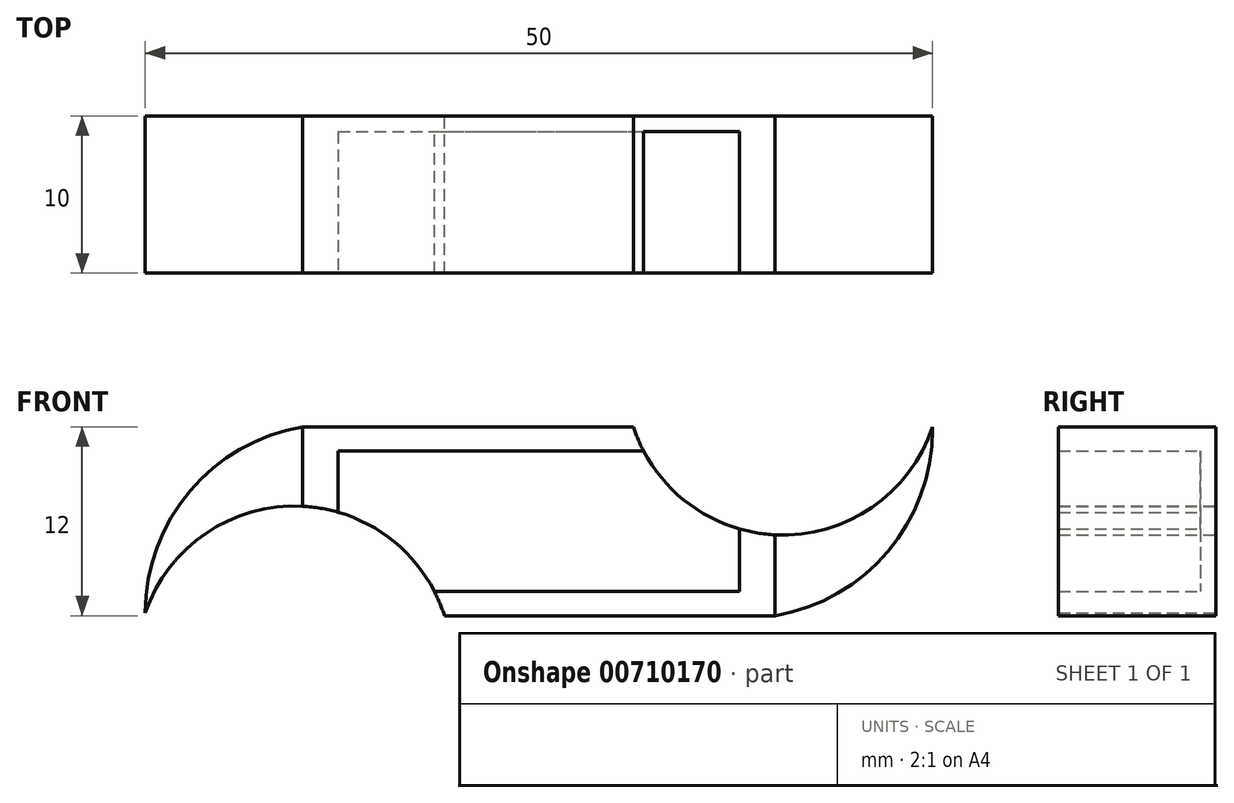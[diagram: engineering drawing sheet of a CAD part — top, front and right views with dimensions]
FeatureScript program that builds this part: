
annotation { "Feature Type Name" : "Feature", "Feature Type Description" : "" }
export const myFeature = defineFeature(function(context is Context, id is Id, definition is map)
    precondition{}
    {
        {
            var Q0;
            Q0=qCreatedBy(makeId("Top.planeOp"),FACE);
            var sketch = newSketch(context, id + "F0", { "sketchPlane" : qUnion([Q0])});
            skLineSegment(sketch, "E0", {"start": v(0, 0) * mm, "end": v(25.5, 0) * mm});
            skLineSegment(sketch, "E1", {"start": v(25.5, 0) * mm, "end": v(25.5, 8.9) * mm});
            skLineSegment(sketch, "E2", {"start": v(25.5, 8.9) * mm, "end": v(0, 8.9) * mm});
            skLineSegment(sketch, "E3", {"start": v(0, 8.9) * mm, "end": v(0, 0) * mm});
            skSolve(sketch);
        }
        {
            var Q0;
            Q0=makeQuery(id+"F0.imprint","IMPRINT",FACE,{"disambiguationData":[TD([[makeQuery(id+"F0.imprint","IMPRINT",EDGE,{"derivedFrom":sQuery(id+"F0.wireOp",EDGE,"E0")}),1.0]])]});
            extrude(context, id + "F1", {"entities" : qUnion([Q0]), "depth" : 8.9 * mm, "offsetDistance" : 25 * mm});
        }
        {
            var Q0;
            Q0=makeQuery(id+"F1.opExtrude","SWEPT_FACE",FACE,{"disambiguationData":[OSD([sQuery(id+"F0.wireOp",EDGE,"E0")])]});
            var sketch = newSketch(context, id + "F2", { "sketchPlane" : qUnion([Q0])});
            skLineSegment(sketch, "E4.bottom", {"start": v(-2.25, 10.45) * mm, "end": v(27.75, 10.45) * mm});
            skLineSegment(sketch, "E4.top", {"start": v(-2.25, -1.55) * mm, "end": v(27.75, -1.55) * mm});
            skLineSegment(sketch, "E4.left", {"start": v(-2.25, 10.45) * mm, "end": v(-2.25, -1.55) * mm});
            skLineSegment(sketch, "E4.right", {"start": v(27.75, 10.45) * mm, "end": v(27.75, -1.55) * mm});
            skPoint(sketch, "E4.middle", {"position": v(12.75, 4.45) * mm});
            skSolve(sketch);
        }
        {
            var Q0;
            {var subQ0=sQuery(id+"F0.wireOp",EDGE,"E0");Q0=makeQuery(id+"F2.imprint","IMPRINT",FACE,{"disambiguationData":[TD([[makeQuery(id+"F2.imprint","IMPRINT",EDGE,{"derivedFrom":makeQuery(id+"F1.opExtrude","CAP_EDGE",EDGE,{"disambiguationData":[OSD([subQ0])],"isStart":true})}),1.0]])]});}
            var Q1;
            Q1=makeQuery(id+"F2.imprint","IMPRINT",FACE,{"disambiguationData":[TD([[makeQuery(id+"F2.imprint","IMPRINT",EDGE,{"derivedFrom":sQuery(id+"F2.wireOp",EDGE,"E4.bottom")}),-1.0]])]});
            extrude(context, id + "F3", {"entities" : qUnion([Q0, Q1]), "oppositeDirection" : true, "depth" : 10 * mm, "offsetDistance" : 25 * mm});
        }
        {
            var Q0;
            Q0=makeQuery(id+"F1.opExtrude","SWEPT_FACE",FACE,{"disambiguationData":[OSD([sQuery(id+"F0.wireOp",EDGE,"E0")])]});
            extrude(context, id + "F4", {"entities" : qUnion([Q0]), "operationType" : NewBodyOperationType.REMOVE, "oppositeDirection" : true, "depth" : 9 * mm, "offsetDistance" : 25 * mm});
        }
        {
            var Q0;
            Q0=makeQuery(id+"F3.opExtrude","SWEPT_FACE",FACE,{"disambiguationData":[OSD([sQuery(id+"F2.wireOp",EDGE,"E4.left")])]});
            extrude(context, id + "F5", {"entities" : qUnion([Q0]), "depth" : 10 * mm, "offsetDistance" : 25 * mm});
        }
        {
            var Q0;
            Q0=makeQuery(id+"F3.opExtrude","SWEPT_FACE",FACE,{"disambiguationData":[OSD([sQuery(id+"F2.wireOp",EDGE,"E4.right")])]});
            extrude(context, id + "F6", {"entities" : qUnion([Q0]), "depth" : 10 * mm, "offsetDistance" : 25 * mm});
        }
        {
            var Q0;
            Q0=makeQuery(id+"F3.opExtrude","SWEPT_FACE",FACE,{"disambiguationData":[OSD([sQuery(id+"F2.wireOp",EDGE,"E4.bottom")])]});
            var sketch = newSketch(context, id + "F7", { "sketchPlane" : qUnion([Q0])});
            skLineSegment(sketch, "E5", {"start": v(12.75, 0) * mm, "end": v(18.75, 0) * mm});
            skLineSegment(sketch, "E6", {"start": v(18.75, 0) * mm, "end": v(18.75, 10) * mm});
            skLineSegment(sketch, "E7", {"start": v(18.75, 10) * mm, "end": v(12.75, 10) * mm});
            skLineSegment(sketch, "E8", {"start": v(12.75, 10) * mm, "end": v(6.75, 10) * mm});
            skLineSegment(sketch, "E9", {"start": v(6.75, 10) * mm, "end": v(6.75, 0) * mm});
            skLineSegment(sketch, "E10", {"start": v(12.75, 0) * mm, "end": v(6.75, 0) * mm});
            skSolve(sketch);
        }
        {
            var Q0;
            Q0=makeQuery(id+"F3.opExtrude","SWEPT_FACE",FACE,{"disambiguationData":[OSD([sQuery(id+"F2.wireOp",EDGE,"E4.top")])]});
            var sketch = newSketch(context, id + "F8", { "sketchPlane" : qUnion([Q0])});
            skLineSegment(sketch, "E11", {"start": v(12.75, -10) * mm, "end": v(18.75, -10) * mm});
            skLineSegment(sketch, "E12", {"start": v(18.75, -10) * mm, "end": v(18.75, 0) * mm});
            skLineSegment(sketch, "E13", {"start": v(12.75, 0) * mm, "end": v(18.75, 0) * mm});
            skLineSegment(sketch, "E14", {"start": v(12.75, 0) * mm, "end": v(6.75, 0) * mm});
            skLineSegment(sketch, "E15", {"start": v(6.75, 0) * mm, "end": v(6.75, -10) * mm});
            skLineSegment(sketch, "E16", {"start": v(6.75, -10) * mm, "end": v(12.75, -10) * mm});
            skSolve(sketch);
        }
        {
            var Q0;
            Q0=makeQuery(id+"FosGmJq5SILQGFZ_5.opExtrude","CAP_EDGE",EDGE,{"disambiguationData":[OSD([sQuery(id+"F8.wireOp",EDGE,"E15")])],"isStart":false});
            var Q1;
            Q1=makeQuery(id+"F5.opExtrude","CAP_EDGE",EDGE,{"disambiguationData":[OSD([sQuery(id+"F2.wireOp",EDGE,"E4.bottom"),sQuery(id+"F2.wireOp",EDGE,"E4.left")])],"isStart":false});
            var Q2;
            Q2=makeQuery(id+"FqWK5za6CKHgtiD_4.opExtrude","CAP_EDGE",EDGE,{"disambiguationData":[OSD([sQuery(id+"F7.wireOp",EDGE,"E6")])],"isStart":false});
            var Q3;
            Q3=makeQuery(id+"F6.opExtrude","CAP_EDGE",EDGE,{"disambiguationData":[OSD([sQuery(id+"F2.wireOp",EDGE,"E4.top"),sQuery(id+"F2.wireOp",EDGE,"E4.right")])],"isStart":false});
            fillet(context, id + "F9", {"entities" : qUnion([Q0, Q1, Q2, Q3]), "radius" : 12 * mm, "tangentPropagation" : true, "allowEdgeOverflow" : false});
        }
        {
            var Q0;
            Q0=makeQuery(id+"FosGmJq5SILQGFZ_5.boolean.opBoolean","MERGE",FACE,{"derivedFrom":[makeQuery(id+"FqWK5za6CKHgtiD_4.boolean.opBoolean","MERGE",FACE,{"derivedFrom":[makeQuery(id+"F3.opExtrude","CAP_FACE",FACE,{"disambiguationData":[OSD([sQuery(id+"F2.wireOp",EDGE,"E4.bottom"),sQuery(id+"F2.wireOp",EDGE,"E4.top"),sQuery(id+"F2.wireOp",EDGE,"E4.left"),sQuery(id+"F2.wireOp",EDGE,"E4.right")])],"isStart":false}),makeQuery(id+"FqWK5za6CKHgtiD_4.opExtrude","SWEPT_FACE",FACE,{"disambiguationData":[OSD([sQuery(id+"F7.wireOp",EDGE,"E7"),sQuery(id+"F7.wireOp",EDGE,"E8")])]})]}),makeQuery(id+"FosGmJq5SILQGFZ_5.opExtrude","SWEPT_FACE",FACE,{"disambiguationData":[OSD([sQuery(id+"F8.wireOp",EDGE,"E11"),sQuery(id+"F8.wireOp",EDGE,"E16")])]})]});
            var sketch = newSketch(context, id + "F10", { "sketchPlane" : qUnion([Q0])});
            skPoint(sketch, "E17.0", {"position": v(-12.75, 10.45) * mm});
            skLineSegment(sketch, "E18", {"start": v(-18.75, 10.45) * mm, "end": v(-18.75, -1.55) * mm});
            skLineSegment(sketch, "E19", {"start": v(-18.75, -1.55) * mm, "end": v(-6.75, -1.55) * mm});
            skLineSegment(sketch, "E20", {"start": v(-6.75, -1.55) * mm, "end": v(-6.75, 10.45) * mm});
            skLineSegment(sketch, "E21", {"start": v(-6.75, 10.45) * mm, "end": v(-18.75, 10.45) * mm});
            skLineSegment(sketch, "E22.0.0", {"start": v(12.25, -1.55) * mm, "end": v(12.25, -1.38) * mm});
            skArc(sketch, "E22.0.1", {"start": v(12.25, -1.38) * mm, "mid": v(9.42, 6.36) * mm, "end": v(2.25, 10.45) * mm});
            skLineSegment(sketch, "E22.0.2", {"start": v(2.25, 10.45) * mm, "end": v(2.25, -1.55) * mm});
            skLineSegment(sketch, "E22.0.3", {"start": v(2.25, -1.55) * mm, "end": v(12.25, -1.55) * mm});
            skLineSegment(sketch, "E23.0.0", {"start": v(-37.75, 10.45) * mm, "end": v(-37.75, 10.28) * mm});
            skArc(sketch, "E23.0.1", {"start": v(-37.75, 10.28) * mm, "mid": v(-34.92, 2.54) * mm, "end": v(-27.75, -1.55) * mm});
            skLineSegment(sketch, "E23.0.2", {"start": v(-27.75, -1.55) * mm, "end": v(-27.75, 10.45) * mm});
            skLineSegment(sketch, "E23.0.3", {"start": v(-27.75, 10.45) * mm, "end": v(-37.75, 10.45) * mm});
            skLineSegment(sketch, "E24.0.0", {"start": v(-18.75, -1.55) * mm, "end": v(-18.75, -20.55) * mm});
            skArc(sketch, "E24.0.1", {"start": v(-18.75, -20.55) * mm, "mid": v(-10.26, -17.04) * mm, "end": v(-6.75, -8.55) * mm});
            skLineSegment(sketch, "E24.0.2", {"start": v(-6.75, -8.55) * mm, "end": v(-6.75, -1.55) * mm});
            skLineSegment(sketch, "E24.0.3", {"start": v(-6.75, -1.55) * mm, "end": v(2.25, -1.55) * mm});
            skLineSegment(sketch, "E24.0.4", {"start": v(2.25, -1.55) * mm, "end": v(2.25, 10.45) * mm});
            skLineSegment(sketch, "E24.0.5", {"start": v(2.25, 10.45) * mm, "end": v(-6.75, 10.45) * mm});
            skLineSegment(sketch, "E24.0.6", {"start": v(-6.75, 10.45) * mm, "end": v(-6.75, 29.45) * mm});
            skArc(sketch, "E24.0.7", {"start": v(-6.75, 29.45) * mm, "mid": v(-15.24, 25.94) * mm, "end": v(-18.75, 17.45) * mm});
            skLineSegment(sketch, "E24.0.8", {"start": v(-18.75, 17.45) * mm, "end": v(-18.75, 10.45) * mm});
            skLineSegment(sketch, "E24.0.9", {"start": v(-18.75, 10.45) * mm, "end": v(-27.75, 10.45) * mm});
            skLineSegment(sketch, "E24.0.10", {"start": v(-27.75, 10.45) * mm, "end": v(-27.75, -1.55) * mm});
            skLineSegment(sketch, "E24.0.11", {"start": v(-27.75, -1.55) * mm, "end": v(-18.75, -1.55) * mm});
            skArc(sketch, "E25", {"start": v(-6.75, 29.45) * mm, "mid": v(-13.63, 19.95) * mm, "end": v(-6.75, 10.45) * mm});
            skArc(sketch, "E26", {"start": v(12.25, -1.38) * mm, "mid": v(2.69, 5.41) * mm, "end": v(-6.75, -1.55) * mm});
            skArc(sketch, "E27", {"start": v(-18.75, -20.55) * mm, "mid": v(-11.87, -11.05) * mm, "end": v(-18.75, -1.55) * mm});
            skArc(sketch, "E28", {"start": v(-37.75, 10.45) * mm, "mid": v(-28.25, 3.57) * mm, "end": v(-18.75, 10.45) * mm});
            skSolve(sketch);
        }
        {
            var Q0;
            {var subQ0=sQuery(id+"F10.wireOp",EDGE,"E23.0.3");Q0=makeQuery(id+"F10.imprint","IMPRINT",FACE,{"disambiguationData":[TD([[makeQuery(id+"F10.imprint","IMPRINT",EDGE,{"derivedFrom":subQ0}),1.0]])]});}
            var Q1;
            {var subQ0=sQuery(id+"F10.wireOp",EDGE,"E24.0.9");Q1=makeQuery(id+"F10.imprint","IMPRINT",FACE,{"disambiguationData":[TD([[makeQuery(id+"F10.imprint","IMPRINT",EDGE,{"derivedFrom":subQ0}),1.0]])]});}
            var Q2;
            Q2=makeQuery(id+"F10.imprint","IMPRINT",FACE,{"disambiguationData":[TD([[makeQuery(id+"F10.imprint","IMPRINT",EDGE,{"derivedFrom":sQuery(id+"F10.wireOp",EDGE,"E24.0.6")}),-1.0]])]});
            var Q3;
            {var subQ0=sQuery(id+"F10.wireOp",EDGE,"E22.0.0");Q3=makeQuery(id+"F10.imprint","IMPRINT",FACE,{"disambiguationData":[TD([[makeQuery(id+"F10.imprint","IMPRINT",EDGE,{"derivedFrom":subQ0}),1.0]])]});}
            var Q4;
            {var subQ0=sQuery(id+"F10.wireOp",EDGE,"E24.0.3");Q4=makeQuery(id+"F10.imprint","IMPRINT",FACE,{"disambiguationData":[TD([[makeQuery(id+"F10.imprint","IMPRINT",EDGE,{"derivedFrom":subQ0}),-1.0]])]});}
            var Q5;
            Q5=makeQuery(id+"F10.imprint","IMPRINT",FACE,{"disambiguationData":[TD([[makeQuery(id+"F10.imprint","IMPRINT",EDGE,{"derivedFrom":sQuery(id+"F10.wireOp",EDGE,"E24.0.0")}),-1.0]])]});
            extrude(context, id + "F11", {"entities" : qUnion([Q0, Q1, Q2, Q3, Q4, Q5]), "operationType" : NewBodyOperationType.REMOVE, "oppositeDirection" : true, "depth" : 10 * mm, "offsetDistance" : 25 * mm});
        }
    });
